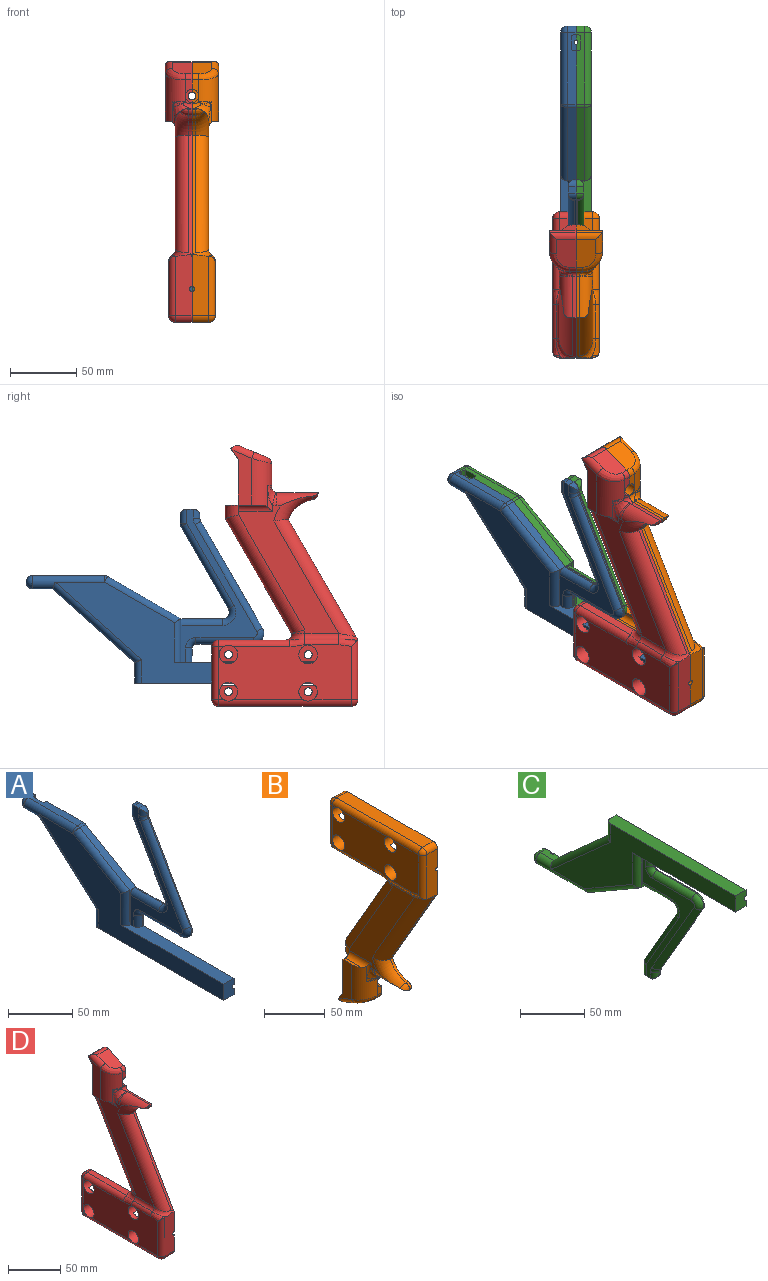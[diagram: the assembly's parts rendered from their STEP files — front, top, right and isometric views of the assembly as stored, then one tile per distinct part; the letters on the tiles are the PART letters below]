
ASSEMBLY  parts=4 mates=3
PART A: 56 faces, bbox 14.1x225x131.1 mm
  f0: plane 53.9x6.5mm, normal (0,0,1), area 312.7mm2, adj f41,f45,f48,f49,f50,f51,f54,f55
  f1: plane 115.6x57.43mm, normal (-1,0,0), area 1150.5mm2, adj f5,f18,f19,f23,f24,f25,f26,f27
  f2: plane 31.34x1mm, normal (0,0,1), area 31.3mm2, adj f17,f35,f36,f55
  f3: plane 61.92x35.75mm, normal (0,0.87,-0.5), area 71.5mm2, adj f33,f36,f39,f55
  f4: plane 5.68x1mm, normal (0,1,0), area 5.7mm2, adj f32,f33,f34,f55
  f5: plane 6x5mm, normal (0,0,1), area 30mm2, adj f1,f30,f32,f55
  f6: plane 1.66x1mm, normal (0,-1,0), area 1.7mm2, adj f28,f30,f31,f55
  f7: plane 80.44x46.44mm, normal (0,-0.87,0.5), area 92.9mm2, adj f8,f27,f31,f55
  f8: cylinder r=8mm len=12mm, axis (-1,0,0), area 16.8mm2, adj f7,f9,f26,f55
  f9: plane 43.14x1mm, normal (0,0,-1), area 43.1mm2, adj f8,f10,f25,f55
  f10: cylinder r=3mm len=3mm, axis (-1,0,0), area 4.7mm2, adj f9,f11,f24,f55
  f11: plane 11x1mm, normal (0,-1,0), area 11mm2, adj f10,f19,f23,f55
  f12: plane 15.5x11.5mm, normal (0,-1,0), area 172mm2, adj f13,f19,f20,f21,f55
  f13: plane 143x11.5mm, normal (0,0,-1), area 1639.1mm2, adj f12,f14,f20,f44,f55
  f14: plane 15.5x6.5mm, normal (0,1,0), area 100.7mm2, adj f13,f15,f44,f55
  f15: plane 62x55.6mm, normal (0,0.67,-0.74), area 541.3mm2, adj f14,f16,f46,f55
  f16: plane 15x6.5mm, normal (0,0,-1), area 94mm2, adj f15,f45,f48,f53,f54,f55
  f17: plane 55.31x31.93mm, normal (0,-0.5,0.87), area 415.1mm2, adj f2,f18,f41,f42,f55
  f18: plane 33x5.5mm, normal (0,-1,0), area 21.9mm2, adj f1,f17,f19,f35,f40
  f19: plane 113.29x11.5mm, normal (0,0,1), area 1206.3mm2, adj f1,f11,f12,f18,f20,f23,f40,f55
  f20: plane 203.09x76.1mm, normal (-1,0,0), area 4731mm2, adj f12,f13,f19,f40,f42,f44,f45,f46
  f21: cylinder r=2mm len=25mm, axis (0,-1,0), area 157.1mm2, adj f12,f22,f55
  f22: plane 4x2mm, normal (0,-1,0), area 6.3mm2, adj f21,f55
  f23: cylinder r=5mm len=11mm, axis (0,0,-1), area 86.4mm2, adj f1,f11,f19,f24
  f24: torus R=8mm, axis (1,0,0), area 59.4mm2, adj f1,f10,f23,f25
  f25: cylinder r=5mm len=43.14mm, axis (0,1,0), area 338.8mm2, adj f1,f9,f24,f26
  f26: torus R=3mm, axis (1,0,0), area 101.7mm2, adj f1,f8,f25,f27
  f27: cylinder r=5mm len=82.94mm, axis (0,-0.5,-0.87), area 729.5mm2, adj f1,f7,f26,f29
  f28: cylinder r=5mm len=6.66mm, axis (0,0,-1), area 38mm2, adj f1,f6,f29,f30
  f29: torus R=10mm, axis (1,0,0), area 28mm2, adj f1,f27,f28,f31
  f30: cylinder r=5mm len=6mm, axis (-1,0,0), area 32.9mm2, adj f5,f6,f28,f55
  f31: cylinder r=5mm len=2.5mm, axis (1,0,0), area 2.6mm2, adj f6,f7,f29,f55
  f32: cylinder r=5mm len=6mm, axis (-1,0,0), area 32.9mm2, adj f4,f5,f34,f55
  f33: cylinder r=5mm len=2.5mm, axis (-1,0,0), area 2.6mm2, adj f3,f4,f37,f55
  f34: cylinder r=5mm len=10.68mm, axis (0,0,1), area 69.6mm2, adj f1,f4,f32,f37
  f35: cylinder r=5mm len=31.34mm, axis (0,-1,0), area 246.1mm2, adj f1,f2,f18,f38
  f36: cylinder r=5mm len=7.5mm, axis (1,0,0), area 10.5mm2, adj f2,f3,f38,f55
  f37: sphere r=5mm, area 13.1mm2, adj f33,f34,f39
  f38: torus R=10mm, axis (1,0,0), area 112.1mm2, adj f1,f35,f36,f39
  f39: cylinder r=5mm len=64.42mm, axis (0,0.5,0.87), area 561.6mm2, adj f1,f3,f37,f38
  f40: cylinder r=5mm len=33mm, axis (0,0,-1), area 250.9mm2, adj f18,f19,f20,f42
  f41: cylinder r=5mm len=6.5mm, axis (-1,0,0), area 17mm2, adj f0,f17,f43,f55
  f42: cylinder r=5mm len=57.81mm, axis (0,-0.87,-0.5), area 493.4mm2, adj f17,f20,f40,f43
  f43: sphere r=5mm, area 13.1mm2, adj f41,f42,f45
  f44: cylinder r=5mm len=17.73mm, axis (0,0,1), area 128.1mm2, adj f13,f14,f20,f46
  f45: cylinder r=5mm len=53.9mm, axis (0,-1,0), area 546.6mm2, adj f0,f16,f20,f43,f46,f47
  f46: cylinder r=5mm len=68.42mm, axis (0,0.74,0.67), area 665.9mm2, adj f15,f20,f44,f45
  f47: sphere r=5mm, area 78.5mm2, adj f45,f48
  f48: cylinder r=5mm len=10mm, axis (-1,0,0), area 102.1mm2, adj f0,f16,f47,f54
  f49: cylinder r=5.54mm len=5mm, axis (0,0,1), area 16.9mm2, adj f0,f50,f52,f54
  f50: plane 10.5x5mm, normal (1,0,0), area 52.5mm2, adj f0,f49,f51,f52
  f51: cylinder r=5.54mm len=5mm, axis (0,0,1), area 16.9mm2, adj f0,f50,f52,f55
  f52: plane 12.5x3.18mm, normal (0,0,1), area 34.1mm2, adj f49,f50,f51,f53,f54,f55
  f53: cylinder r=1.5mm len=5mm, axis (0,0,1), area 23.6mm2, adj f16,f52,f54,f55
  f54: plane 10.76x10mm, normal (1,0,0), area 74.6mm2, adj f0,f16,f48,f49,f52,f53
  f55: plane 211.24x131.1mm, normal (1,0,0), area 8535.1mm2, adj f0,f2,f3,f4,f5,f6,f7,f8
PART B: 92 faces, bbox 27.3x113x198.3 mm
  f0: plane 53.82x6.5mm, normal (0,0,-1), area 336.5mm2, adj f1,f2,f10,f83
  f1: torus R=15mm, axis (0,0,-1), area 106.8mm2, adj f0,f47,f52,f64,f79,f83
  f2: cylinder r=5mm len=6.5mm, axis (-1,0,0), area 51.1mm2, adj f0,f4,f62,f83
  f3: plane 105x12.5mm, normal (0,0,1), area 1169mm2, adj f4,f5,f6,f7,f8,f77,f78,f80
  f4: plane 11x6.5mm, normal (0,1,0), area 71.5mm2, adj f2,f3,f60,f83
  f5: plane 14x12mm, normal (-1,0,0), area 112.2mm2, adj f3,f6,f68
  f6: cylinder r=7mm len=14mm, axis (-1,0,0), area 388.9mm2, adj f3,f5,f10,f31,f77
  f7: plane 14x12mm, normal (-1,0,0), area 112.2mm2, adj f3,f8,f75
  f8: cylinder r=7mm len=14mm, axis (-1,0,0), area 385.6mm2, adj f3,f7,f31,f77
  f9: cylinder r=5mm len=100mm, axis (0,1,0), area 775.6mm2, adj f29,f31,f56,f57,f71,f74
  f10: cylinder r=5mm len=53.82mm, axis (0,-1,0), area 417.8mm2, adj f0,f6,f31,f62,f64
  f11: plane 5.5x5mm, normal (0,-1,0), area 7mm2, adj f32,f38,f40,f67,f89
  f12: plane 12.16x5mm, normal (0,-1,0), area 41.2mm2, adj f32,f35,f67,f91
  f13: plane 31x2.5mm, normal (0,0,-1), area 77.5mm2, adj f14,f38,f43,f89
  f14: plane 4.12x0.4mm, normal (0,-1,0), area 1.4mm2, adj f13,f43,f50,f51,f89
  f15: cylinder r=24mm len=18.33mm, axis (-1,0,0), area 61.6mm2, adj f16,f42,f50,f89
  f16: plane 89.82x51.9mm, normal (0,-0.87,-0.5), area 257.3mm2, adj f15,f41,f53,f89
  f17: plane 86.6x50mm, normal (0,0.87,0.5), area 250mm2, adj f18,f48,f79,f89
  f18: plane 10x2.5mm, normal (0,1,0), area 25mm2, adj f17,f19,f49,f89
  f19: plane 12.5x10mm, normal (0,0,-1), area 103.5mm2, adj f18,f22,f49,f89
  f20: plane 96.52x75.57mm, normal (-1,0,0), area 2243.3mm2, adj f37,f39,f41,f42,f43,f44,f47,f48
  f21: plane 18.29x2.5mm, normal (0,0,1), area 39.1mm2, adj f22,f26,f32,f37
  f22: plane 39.5x20mm, normal (0,1,0), area 681.2mm2, adj f19,f21,f23,f26,f37,f49,f65,f89
  f23: plane 20x8.2mm, normal (0,0.82,0.57), area 200mm2, adj f22,f24,f26,f34,f91
  f24: plane 19.99x1.89mm, normal (0,0.57,-0.82), area 44.3mm2, adj f23,f34,f36,f91
  f25: plane 21.02x15mm, normal (0,-0.38,-0.92), area 318.2mm2, adj f33,f34,f35,f36,f91
  f26: plane 41.5x14.9mm, normal (-1,0,0), area 386.1mm2, adj f21,f22,f23,f32,f34
  f27: plane 1.71x1.52mm, normal (0,0,-1), area 1.2mm2, adj f28,f53,f58
  f28: plane 45.92x12.5mm, normal (0,-1,0), area 562.1mm2, adj f27,f53,f54,f59,f88,f89,f90
  f29: plane 100x12.5mm, normal (0,0,1), area 1250mm2, adj f9,f54,f55,f90
  f30: plane 12.5x11mm, normal (0,1,0), area 137.5mm2, adj f55,f60,f76,f90
  f31: plane 100x41.34mm, normal (-1,0,0), area 3449mm2, adj f6,f8,f9,f10,f59,f60,f61,f63
  f32: cylinder r=15mm len=36.41mm, axis (0,0,1), area 638.9mm2, adj f11,f12,f21,f26,f33,f37,f39,f40
  f33: bspline ~17.61x15.14mm, area 137.9mm2, adj f25,f32,f34,f35
  f34: cylinder r=5mm len=17.95mm, axis (0,-0.92,0.38), area 118mm2, adj f23,f24,f25,f26,f33,f36
  f35: cylinder r=5mm len=5mm, axis (-1,0,0), area 29.4mm2, adj f12,f25,f33,f91
  f36: cylinder r=5mm len=19.22mm, axis (-1,0,0), area 85.9mm2, adj f24,f25,f34,f91
  f37: cylinder r=5mm len=25.61mm, axis (0,1,0), area 173.5mm2, adj f20,f21,f22,f32,f39
  f38: cylinder r=4mm len=6.9mm, axis (-1,0,0), area 28.7mm2, adj f11,f13,f40,f44,f45,f89
  f39: cylinder r=5mm len=19.5mm, axis (0,0,1), area 41.9mm2, adj f20,f32,f37,f45,f46
  f40: torus R=20mm, axis (0,0,-1), area 9.4mm2, adj f11,f32,f38,f45,f46
  f41: cylinder r=10mm len=97.19mm, axis (0,-0.5,0.87), area 1570mm2, adj f16,f20,f42,f53
  f42: torus R=34mm, axis (1,0,0), area 377.9mm2, adj f15,f20,f41,f43,f51
  f43: cylinder r=10mm len=31mm, axis (0,-1,0), area 328mm2, adj f13,f14,f20,f42,f44,f51
  f44: torus R=14mm, axis (1,0,0), area 29.3mm2, adj f20,f38,f43,f45
  f45: bspline ~15.13x11.48mm, area 78.3mm2, adj f38,f39,f40,f44,f46
  f46: bspline ~7.09x5.76mm, area 8.6mm2, adj f39,f40,f45
  f47: cylinder r=10mm len=10mm, axis (0,0,-1), area 21mm2, adj f1,f20,f48
  f48: cylinder r=10mm len=93.92mm, axis (0,0.5,-0.87), area 1570.8mm2, adj f17,f20,f47,f49
  f49: cylinder r=10mm len=10mm, axis (0,0,-1), area 136mm2, adj f18,f19,f20,f22,f48
  f50: cylinder r=5mm len=4.93mm, axis (-1,0,0), area 17.5mm2, adj f14,f15,f51,f89
  f51: bspline ~9.16x6.8mm, area 39.1mm2, adj f14,f42,f43,f50
  f52: cylinder r=5mm len=25.57mm, axis (0,-1,0), area 133.9mm2, adj f1,f20,f53,f63
  f53: bspline ~18.33x17.32mm, area 95mm2, adj f16,f27,f28,f41,f52,f61,f89
  f54: cylinder r=5mm len=12.5mm, axis (-1,0,0), area 98.2mm2, adj f28,f29,f56,f90
  f55: cylinder r=5mm len=12.5mm, axis (-1,0,0), area 98.2mm2, adj f29,f30,f57,f90
  f56: sphere r=5mm, area 53.5mm2, adj f9,f54,f59
  f57: sphere r=5mm, area 39.3mm2, adj f9,f55,f60
  f58: cylinder r=5mm len=3.59mm, axis (0,-1,0), area 3.1mm2, adj f27,f59,f61
  f59: cylinder r=5mm len=45mm, axis (0,0,1), area 338.3mm2, adj f28,f31,f56,f58,f61
  f60: cylinder r=5mm len=40mm, axis (0,0,-1), area 314.2mm2, adj f4,f30,f31,f57,f62,f77
  f61: bspline ~16.25x5.68mm, area 74.3mm2, adj f31,f53,f58,f59,f63
  f62: sphere r=5mm, area 25mm2, adj f2,f10,f60
  f63: cylinder r=5mm len=25.57mm, axis (0,-1,0), area 133.9mm2, adj f31,f52,f61,f64
  f64: bspline ~13.38x5.67mm, area 70mm2, adj f1,f10,f31,f63
  f65: cylinder r=3mm len=15mm, axis (0,-1,0), area 141.4mm2, adj f22,f66,f89,f91
  f66: plane 10x5mm, normal (0,-1,0), area 25.1mm2, adj f65,f67,f89,f91
  f67: cylinder r=5mm len=10mm, axis (0,-1,0), area 157.1mm2, adj f11,f12,f66,f89,f91
  f68: cylinder r=3mm len=7.4mm, axis (-1,0,0), area 139.5mm2, adj f5,f89
  f69: cylinder r=3mm len=7.4mm, axis (-1,0,0), area 139.5mm2, adj f70,f90
  f70: plane 14x12mm, normal (-1,0,0), area 112.2mm2, adj f69,f71,f76
  f71: cylinder r=7mm len=14mm, axis (-1,0,0), area 388.9mm2, adj f9,f31,f70,f76,f77
  f72: cylinder r=3mm len=7.4mm, axis (-1,0,0), area 139.5mm2, adj f73,f90
  f73: plane 14x12mm, normal (-1,0,0), area 112.2mm2, adj f72,f74,f76
  f74: cylinder r=7mm len=14mm, axis (-1,0,0), area 388.9mm2, adj f9,f31,f73,f76,f77
  f75: cylinder r=3mm len=7.5mm, axis (-1,0,0), area 141.4mm2, adj f7,f89
  f76: plane 105x12.5mm, normal (0,0,-1), area 1212.5mm2, adj f30,f70,f71,f73,f74,f77,f78,f90
  f77: plane 105x18mm, normal (1,0,0), area 1836mm2, adj f3,f6,f8,f60,f71,f74,f76,f78
  f78: plane 18x12.5mm, normal (0,1,0), area 218.7mm2, adj f3,f76,f77,f88,f89,f90
  f79: plane 7.07x6.07mm, normal (0,1,0), area 37.8mm2, adj f1,f17,f83,f87,f89
  f80: plane 7x2mm, normal (0,1,0), area 14mm2, adj f3,f82,f84,f89
  f81: plane 45x2mm, normal (0,0,-1), area 90mm2, adj f82,f86,f87,f89
  f82: cylinder r=3mm len=3mm, axis (1,0,0), area 9.4mm2, adj f80,f81,f85,f89
  f83: plane 60.06x18.69mm, normal (1,0,0), area 184.7mm2, adj f0,f1,f2,f3,f4,f79,f84,f85
  f84: cylinder r=4mm len=7mm, axis (0,0,1), area 44mm2, adj f3,f80,f83,f85
  f85: torus R=7mm, axis (1,0,0), area 44mm2, adj f82,f83,f84,f86
  f86: cylinder r=4mm len=49mm, axis (0,1,0), area 295.3mm2, adj f81,f83,f85,f87
  f87: cylinder r=4mm len=6mm, axis (-1,0,0), area 25.1mm2, adj f79,f81,f86,f89
  f88: cylinder r=2mm len=5mm, axis (0,-1,0), area 31.4mm2, adj f28,f78,f89,f90
  f89: plane 140.35x102mm, normal (1,0,0), area 6800.7mm2, adj f3,f11,f13,f14,f15,f16,f17,f18
  f90: plane 110x23.25mm, normal (1,0,0), area 1729mm2, adj f28,f29,f30,f54,f55,f69,f72,f76
  f91: plane 30.74x22.89mm, normal (1,0,0), area 452.6mm2, adj f12,f22,f23,f24,f25,f35,f36,f65
PART C: 56 faces, bbox 14.1x225x131.1 mm
  f0: plane 53.9x6.5mm, normal (0,0,-1), area 312.7mm2, adj f41,f45,f48,f49,f50,f51,f54,f55
  f1: plane 115.6x57.43mm, normal (-1,0,0), area 1150.5mm2, adj f5,f18,f19,f23,f24,f25,f26,f27
  f2: plane 31.34x1mm, normal (0,0,-1), area 31.3mm2, adj f17,f35,f36,f55
  f3: plane 61.92x35.75mm, normal (0,0.87,0.5), area 71.5mm2, adj f33,f36,f39,f55
  f4: plane 5.68x1mm, normal (0,1,0), area 5.7mm2, adj f32,f33,f34,f55
  f5: plane 6x5mm, normal (0,0,-1), area 30mm2, adj f1,f30,f32,f55
  f6: plane 1.66x1mm, normal (0,-1,0), area 1.7mm2, adj f28,f30,f31,f55
  f7: plane 80.44x46.44mm, normal (0,-0.87,-0.5), area 92.9mm2, adj f8,f27,f31,f55
  f8: cylinder r=8mm len=12mm, axis (-1,0,0), area 16.8mm2, adj f7,f9,f26,f55
  f9: plane 43.14x1mm, normal (0,0,1), area 43.1mm2, adj f8,f10,f25,f55
  f10: cylinder r=3mm len=3mm, axis (-1,0,0), area 4.7mm2, adj f9,f11,f24,f55
  f11: plane 11x1mm, normal (0,-1,0), area 11mm2, adj f10,f19,f23,f55
  f12: plane 15.5x11.5mm, normal (0,-1,0), area 172mm2, adj f13,f19,f20,f21,f55
  f13: plane 143x11.5mm, normal (0,0,1), area 1639.1mm2, adj f12,f14,f20,f44,f55
  f14: plane 15.5x6.5mm, normal (0,1,0), area 100.8mm2, adj f13,f15,f44,f55
  f15: plane 62x55.6mm, normal (0,0.67,0.74), area 541.3mm2, adj f14,f16,f46,f55
  f16: plane 15x6.5mm, normal (0,0,1), area 94mm2, adj f15,f45,f48,f53,f54,f55
  f17: plane 55.31x31.93mm, normal (0,-0.5,-0.87), area 415.1mm2, adj f2,f18,f41,f42,f55
  f18: plane 33x5.5mm, normal (0,-1,0), area 21.9mm2, adj f1,f17,f19,f35,f40
  f19: plane 113.29x11.5mm, normal (0,0,-1), area 1206.3mm2, adj f1,f11,f12,f18,f20,f23,f40,f55
  f20: plane 203.09x76.1mm, normal (-1,0,0), area 4731mm2, adj f12,f13,f19,f40,f42,f44,f45,f46
  f21: cylinder r=2mm len=25mm, axis (0,-1,0), area 157.1mm2, adj f12,f22,f55
  f22: plane 4x2mm, normal (0,-1,0), area 6.3mm2, adj f21,f55
  f23: cylinder r=5mm len=11mm, axis (0,0,1), area 86.4mm2, adj f1,f11,f19,f24
  f24: torus R=8mm, axis (1,0,0), area 59.4mm2, adj f1,f10,f23,f25
  f25: cylinder r=5mm len=43.14mm, axis (0,1,0), area 338.8mm2, adj f1,f9,f24,f26
  f26: torus R=3mm, axis (1,0,0), area 101.7mm2, adj f1,f8,f25,f27
  f27: cylinder r=5mm len=82.94mm, axis (0,-0.5,0.87), area 729.5mm2, adj f1,f7,f26,f29
  f28: cylinder r=5mm len=6.66mm, axis (0,0,1), area 38mm2, adj f1,f6,f29,f30
  f29: torus R=10mm, axis (1,0,0), area 28mm2, adj f1,f27,f28,f31
  f30: cylinder r=5mm len=6mm, axis (-1,0,0), area 32.9mm2, adj f5,f6,f28,f55
  f31: cylinder r=5mm len=2.5mm, axis (1,0,0), area 2.6mm2, adj f6,f7,f29,f55
  f32: cylinder r=5mm len=6mm, axis (-1,0,0), area 32.9mm2, adj f4,f5,f34,f55
  f33: cylinder r=5mm len=2.5mm, axis (-1,0,0), area 2.6mm2, adj f3,f4,f37,f55
  f34: cylinder r=5mm len=10.68mm, axis (0,0,-1), area 69.6mm2, adj f1,f4,f32,f37
  f35: cylinder r=5mm len=31.34mm, axis (0,-1,0), area 246.1mm2, adj f1,f2,f18,f38
  f36: cylinder r=5mm len=7.5mm, axis (1,0,0), area 10.5mm2, adj f2,f3,f38,f55
  f37: sphere r=5mm, area 13.1mm2, adj f33,f34,f39
  f38: torus R=10mm, axis (1,0,0), area 112.1mm2, adj f1,f35,f36,f39
  f39: cylinder r=5mm len=64.42mm, axis (0,0.5,-0.87), area 561.6mm2, adj f1,f3,f37,f38
  f40: cylinder r=5mm len=33mm, axis (0,0,1), area 250.9mm2, adj f18,f19,f20,f42
  f41: cylinder r=5mm len=6.5mm, axis (-1,0,0), area 17mm2, adj f0,f17,f43,f55
  f42: cylinder r=5mm len=57.81mm, axis (0,-0.87,0.5), area 493.4mm2, adj f17,f20,f40,f43
  f43: sphere r=5mm, area 13.1mm2, adj f41,f42,f45
  f44: cylinder r=5mm len=17.73mm, axis (0,0,-1), area 128.1mm2, adj f13,f14,f20,f46
  f45: cylinder r=5mm len=53.9mm, axis (0,-1,0), area 546.6mm2, adj f0,f16,f20,f43,f46,f47
  f46: cylinder r=5mm len=68.42mm, axis (0,0.74,-0.67), area 665.9mm2, adj f15,f20,f44,f45
  f47: sphere r=5mm, area 78.5mm2, adj f45,f48
  f48: cylinder r=5mm len=10mm, axis (-1,0,0), area 102.1mm2, adj f0,f16,f47,f54
  f49: cylinder r=5.54mm len=5mm, axis (0,0,-1), area 16.9mm2, adj f0,f50,f52,f54
  f50: plane 10.5x5mm, normal (1,0,0), area 52.5mm2, adj f0,f49,f51,f52
  f51: cylinder r=5.54mm len=5mm, axis (0,0,-1), area 16.9mm2, adj f0,f50,f52,f55
  f52: plane 12.5x3.18mm, normal (0,0,-1), area 34.1mm2, adj f49,f50,f51,f53,f54,f55
  f53: cylinder r=1.5mm len=5mm, axis (0,0,-1), area 23.6mm2, adj f16,f52,f54,f55
  f54: plane 10.76x10mm, normal (1,0,0), area 74.6mm2, adj f0,f16,f48,f49,f52,f53
  f55: plane 211.24x131.1mm, normal (1,0,0), area 8535.1mm2, adj f0,f2,f3,f4,f5,f6,f7,f8
PART D: 92 faces, bbox 27.3x113x198.3 mm
  f0: plane 53.82x6.5mm, normal (0,0,1), area 336.5mm2, adj f1,f2,f10,f83
  f1: torus R=15mm, axis (0,0,1), area 106.8mm2, adj f0,f47,f52,f64,f79,f83
  f2: cylinder r=5mm len=6.5mm, axis (-1,0,0), area 51.1mm2, adj f0,f4,f62,f83
  f3: plane 105x12.5mm, normal (0,0,-1), area 1169mm2, adj f4,f5,f6,f7,f8,f77,f78,f80
  f4: plane 11x6.5mm, normal (0,1,0), area 71.5mm2, adj f2,f3,f60,f83
  f5: plane 14x12mm, normal (-1,0,0), area 112.2mm2, adj f3,f6,f68
  f6: cylinder r=7mm len=14mm, axis (-1,0,0), area 388.9mm2, adj f3,f5,f10,f31,f77
  f7: plane 14x12mm, normal (-1,0,0), area 112.2mm2, adj f3,f8,f75
  f8: cylinder r=7mm len=14mm, axis (-1,0,0), area 385.6mm2, adj f3,f7,f31,f77
  f9: cylinder r=5mm len=100mm, axis (0,1,0), area 775.6mm2, adj f29,f31,f56,f57,f71,f74
  f10: cylinder r=5mm len=53.82mm, axis (0,-1,0), area 417.8mm2, adj f0,f6,f31,f62,f64
  f11: plane 5.5x5mm, normal (0,-1,0), area 7mm2, adj f32,f38,f40,f67,f89
  f12: plane 12.16x5mm, normal (0,-1,0), area 41.2mm2, adj f32,f35,f67,f91
  f13: plane 31x2.5mm, normal (0,0,1), area 77.5mm2, adj f14,f38,f43,f89
  f14: plane 4.12x0.4mm, normal (0,-1,0), area 1.4mm2, adj f13,f43,f50,f51,f89
  f15: cylinder r=24mm len=18.33mm, axis (-1,0,0), area 61.6mm2, adj f16,f42,f50,f89
  f16: plane 89.82x51.9mm, normal (0,-0.87,0.5), area 257.3mm2, adj f15,f41,f53,f89
  f17: plane 86.6x50mm, normal (0,0.87,-0.5), area 250mm2, adj f18,f48,f79,f89
  f18: plane 10x2.5mm, normal (0,1,0), area 25mm2, adj f17,f19,f49,f89
  f19: plane 12.5x10mm, normal (0,0,1), area 103.5mm2, adj f18,f22,f49,f89
  f20: plane 96.52x75.57mm, normal (-1,0,0), area 2243.3mm2, adj f37,f39,f41,f42,f43,f44,f47,f48
  f21: plane 18.29x2.5mm, normal (0,0,-1), area 39.1mm2, adj f22,f26,f32,f37
  f22: plane 39.5x20mm, normal (0,1,0), area 681.2mm2, adj f19,f21,f23,f26,f37,f49,f65,f89
  f23: plane 20x8.2mm, normal (0,0.82,-0.57), area 200mm2, adj f22,f24,f26,f34,f91
  f24: plane 19.99x1.89mm, normal (0,0.57,0.82), area 44.3mm2, adj f23,f34,f36,f91
  f25: plane 21.02x15mm, normal (0,-0.38,0.92), area 318.2mm2, adj f33,f34,f35,f36,f91
  f26: plane 41.5x14.9mm, normal (-1,0,0), area 386.1mm2, adj f21,f22,f23,f32,f34
  f27: plane 1.71x1.52mm, normal (0,0,1), area 1.2mm2, adj f28,f53,f58
  f28: plane 45.92x12.5mm, normal (0,-1,0), area 562.1mm2, adj f27,f53,f54,f59,f88,f89,f90
  f29: plane 100x12.5mm, normal (0,0,-1), area 1250mm2, adj f9,f54,f55,f90
  f30: plane 12.5x11mm, normal (0,1,0), area 137.5mm2, adj f55,f60,f76,f90
  f31: plane 100x41.34mm, normal (-1,0,0), area 3449mm2, adj f6,f8,f9,f10,f59,f60,f61,f63
  f32: cylinder r=15mm len=36.41mm, axis (0,0,-1), area 638.9mm2, adj f11,f12,f21,f26,f33,f37,f39,f40
  f33: bspline ~15.65x15.07mm, area 137.9mm2, adj f25,f32,f34,f35
  f34: cylinder r=5mm len=17.95mm, axis (0,-0.92,-0.38), area 118mm2, adj f23,f24,f25,f26,f33,f36
  f35: cylinder r=5mm len=5mm, axis (-1,0,0), area 29.4mm2, adj f12,f25,f33,f91
  f36: cylinder r=5mm len=19.22mm, axis (-1,0,0), area 85.9mm2, adj f24,f25,f34,f91
  f37: cylinder r=5mm len=25.61mm, axis (0,1,0), area 173.5mm2, adj f20,f21,f22,f32,f39
  f38: cylinder r=4mm len=6.9mm, axis (-1,0,0), area 28.7mm2, adj f11,f13,f40,f44,f45,f89
  f39: cylinder r=5mm len=19.5mm, axis (0,0,-1), area 41.9mm2, adj f20,f32,f37,f45,f46
  f40: torus R=20mm, axis (0,0,1), area 9.4mm2, adj f11,f32,f38,f45,f46
  f41: cylinder r=10mm len=97.19mm, axis (0,-0.5,-0.87), area 1570mm2, adj f16,f20,f42,f53
  f42: torus R=34mm, axis (1,0,0), area 377.9mm2, adj f15,f20,f41,f43,f51
  f43: cylinder r=10mm len=31mm, axis (0,-1,0), area 328mm2, adj f13,f14,f20,f42,f44,f51
  f44: torus R=14mm, axis (1,0,0), area 29.3mm2, adj f20,f38,f43,f45
  f45: bspline ~15.13x11.48mm, area 78.3mm2, adj f38,f39,f40,f44,f46
  f46: bspline ~7.09x5.76mm, area 8.6mm2, adj f39,f40,f45
  f47: cylinder r=10mm len=10mm, axis (0,0,1), area 21mm2, adj f1,f20,f48
  f48: cylinder r=10mm len=93.92mm, axis (0,0.5,0.87), area 1570.8mm2, adj f17,f20,f47,f49
  f49: cylinder r=10mm len=10mm, axis (0,0,1), area 136mm2, adj f18,f19,f20,f22,f48
  f50: cylinder r=5mm len=4.93mm, axis (-1,0,0), area 17.5mm2, adj f14,f15,f51,f89
  f51: bspline ~9.16x6.8mm, area 39.1mm2, adj f14,f42,f43,f50
  f52: cylinder r=5mm len=25.57mm, axis (0,-1,0), area 133.9mm2, adj f1,f20,f53,f63
  f53: bspline ~18.33x17.32mm, area 95mm2, adj f16,f27,f28,f41,f52,f61,f89
  f54: cylinder r=5mm len=12.5mm, axis (-1,0,0), area 98.2mm2, adj f28,f29,f56,f90
  f55: cylinder r=5mm len=12.5mm, axis (-1,0,0), area 98.2mm2, adj f29,f30,f57,f90
  f56: sphere r=5mm, area 39.3mm2, adj f9,f54,f59
  f57: sphere r=5mm, area 53.5mm2, adj f9,f55,f60
  f58: cylinder r=5mm len=3.59mm, axis (0,-1,0), area 3.1mm2, adj f27,f59,f61
  f59: cylinder r=5mm len=45mm, axis (0,0,-1), area 338.3mm2, adj f28,f31,f56,f58,f61
  f60: cylinder r=5mm len=40mm, axis (0,0,1), area 314.2mm2, adj f4,f30,f31,f57,f62,f77
  f61: bspline ~16.25x5.68mm, area 74.3mm2, adj f31,f53,f58,f59,f63
  f62: sphere r=5mm, area 39.3mm2, adj f2,f10,f60
  f63: cylinder r=5mm len=25.57mm, axis (0,-1,0), area 133.9mm2, adj f31,f52,f61,f64
  f64: bspline ~14.9x5.67mm, area 70mm2, adj f1,f10,f31,f63
  f65: cylinder r=3mm len=15mm, axis (0,-1,0), area 141.4mm2, adj f22,f66,f89,f91
  f66: plane 10x5mm, normal (0,-1,0), area 25.1mm2, adj f65,f67,f89,f91
  f67: cylinder r=5mm len=10mm, axis (0,-1,0), area 157.1mm2, adj f11,f12,f66,f89,f91
  f68: cylinder r=3mm len=7.4mm, axis (-1,0,0), area 139.5mm2, adj f5,f89
  f69: cylinder r=3mm len=7.4mm, axis (-1,0,0), area 139.5mm2, adj f70,f90
  f70: plane 14x12mm, normal (-1,0,0), area 112.2mm2, adj f69,f71,f76
  f71: cylinder r=7mm len=14mm, axis (-1,0,0), area 388.9mm2, adj f9,f31,f70,f76,f77
  f72: cylinder r=3mm len=7.4mm, axis (-1,0,0), area 139.5mm2, adj f73,f90
  f73: plane 14x12mm, normal (-1,0,0), area 112.2mm2, adj f72,f74,f76
  f74: cylinder r=7mm len=14mm, axis (-1,0,0), area 388.9mm2, adj f9,f31,f73,f76,f77
  f75: cylinder r=3mm len=7.5mm, axis (-1,0,0), area 141.4mm2, adj f7,f89
  f76: plane 105x12.5mm, normal (0,0,1), area 1212.5mm2, adj f30,f70,f71,f73,f74,f77,f78,f90
  f77: plane 105x18mm, normal (1,0,0), area 1836mm2, adj f3,f6,f8,f60,f71,f74,f76,f78
  f78: plane 18x12.5mm, normal (0,1,0), area 218.7mm2, adj f3,f76,f77,f88,f89,f90
  f79: plane 7.07x6.07mm, normal (0,1,0), area 37.8mm2, adj f1,f17,f83,f87,f89
  f80: plane 7x2mm, normal (0,1,0), area 14mm2, adj f3,f82,f84,f89
  f81: plane 45x2mm, normal (0,0,1), area 90mm2, adj f82,f86,f87,f89
  f82: cylinder r=3mm len=3mm, axis (1,0,0), area 9.4mm2, adj f80,f81,f85,f89
  f83: plane 60.06x18.69mm, normal (1,0,0), area 184.7mm2, adj f0,f1,f2,f3,f4,f79,f84,f85
  f84: cylinder r=4mm len=7mm, axis (0,0,-1), area 44mm2, adj f3,f80,f83,f85
  f85: torus R=7mm, axis (1,0,0), area 44mm2, adj f82,f83,f84,f86
  f86: cylinder r=4mm len=49mm, axis (0,1,0), area 295.3mm2, adj f81,f83,f85,f87
  f87: cylinder r=4mm len=6mm, axis (-1,0,0), area 25.1mm2, adj f79,f81,f86,f89
  f88: cylinder r=2mm len=5mm, axis (0,-1,0), area 31.4mm2, adj f28,f78,f89,f90
  f89: plane 140.35x102mm, normal (1,0,0), area 6800.7mm2, adj f3,f11,f13,f14,f15,f16,f17,f18
  f90: plane 110x23.25mm, normal (1,0,0), area 1729mm2, adj f28,f29,f30,f54,f55,f69,f72,f76
  f91: plane 30.74x22.89mm, normal (1,0,0), area 452.6mm2, adj f12,f22,f23,f24,f25,f35,f36,f65
PLACE A at identity
PLACE B rot(axis=(0,1,0),180deg) t=(0,0,50)mm
PLACE C rot(axis=(0,1,0),180deg) t=(0,0,50)mm
PLACE D at identity fixed
MATE slider D.f88 <-> A.f21  axis (0,1,0) through (0,-85,-160.85)mm
MATE fastened A.f55 <-> C.f55  axis (1,0,0) through (0,78,-168.6)mm
MATE fastened B.f89 <-> D.f89  axis (-1,0,0) through (0,10,-34.5)mm
